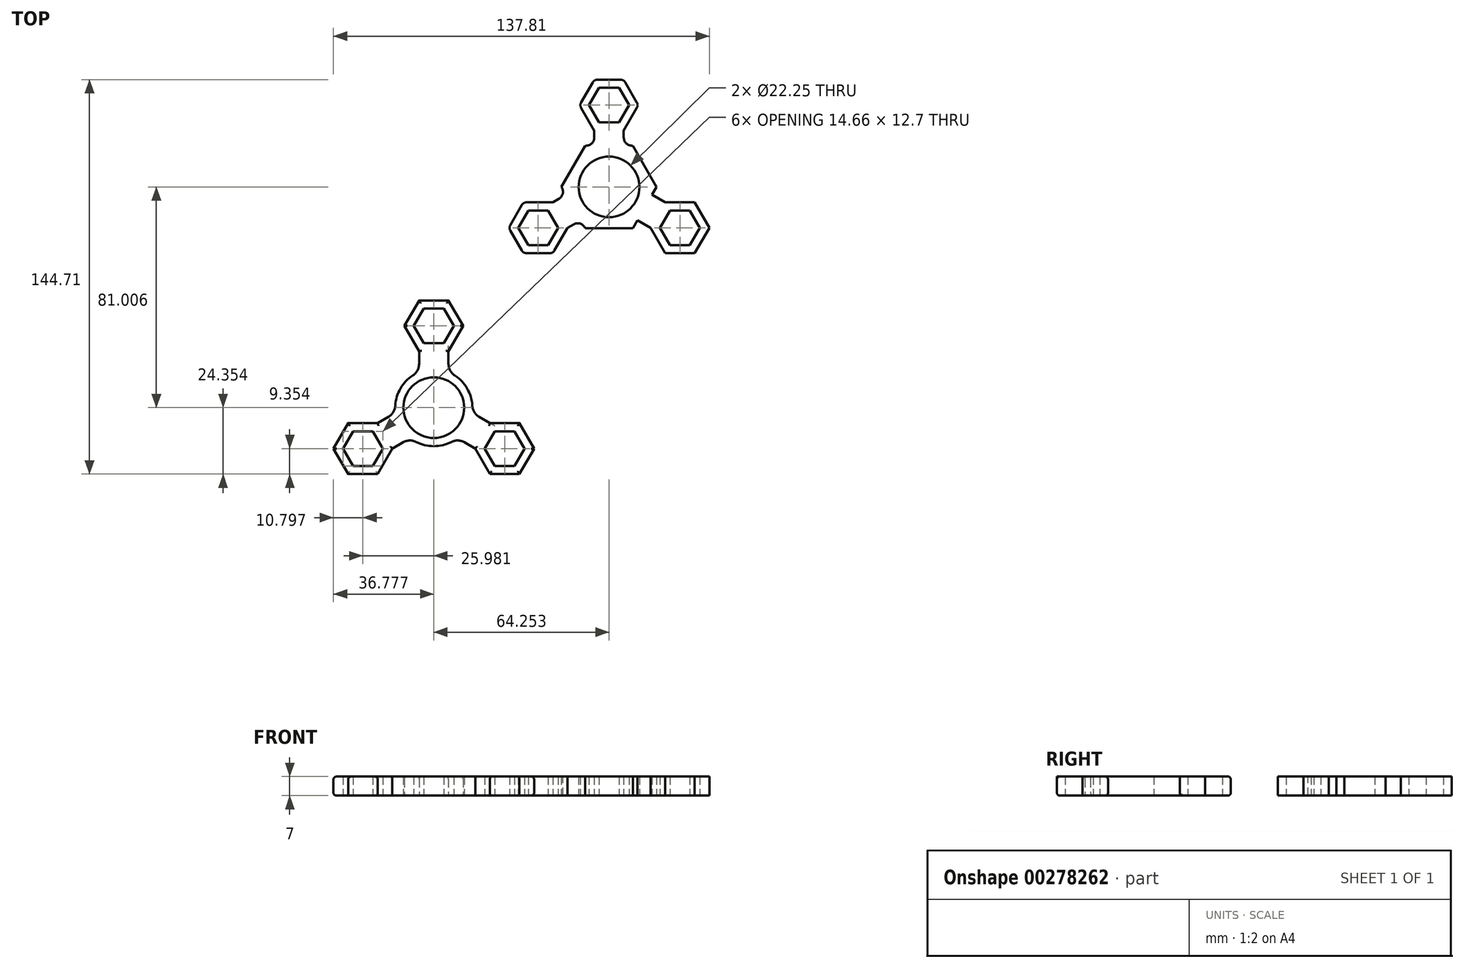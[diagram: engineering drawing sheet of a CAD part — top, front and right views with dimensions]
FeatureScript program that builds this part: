
annotation { "Feature Type Name" : "Feature", "Feature Type Description" : "" }
export const myFeature = defineFeature(function(context is Context, id is Id, definition is map)
    precondition{}
    {
        {
            var Q0;
            Q0=qCreatedBy(makeId("Top.planeOp"),FACE);
            var sketch = newSketch(context, id + "F0", { "sketchPlane" : qUnion([Q0])});
            skCircle(sketch, "E0", {"center": v(-64.25, -81) * mm, "radius": 11.12 * mm});
            skPoint(sketch, "E1.0.midPoint", {"position": v(-64.25, -57.36) * mm});
            skCircle(sketch, "E2.cCircle", {"center": v(-64.25, -51) * mm, "radius": 6.35 * mm, "construction": true});
            skLineSegment(sketch, "E2.0", {"start": v(-67.92, -44.66) * mm, "end": v(-60.59, -44.66) * mm});
            skLineSegment(sketch, "E2.1", {"start": v(-60.59, -44.66) * mm, "end": v(-56.92, -51) * mm});
            skLineSegment(sketch, "E2.2", {"start": v(-56.92, -51) * mm, "end": v(-60.59, -57.36) * mm});
            skLineSegment(sketch, "E2.3", {"start": v(-60.59, -57.36) * mm, "end": v(-67.92, -57.36) * mm});
            skLineSegment(sketch, "E2.4", {"start": v(-67.92, -57.36) * mm, "end": v(-71.58, -51) * mm});
            skLineSegment(sketch, "E2.5", {"start": v(-71.58, -51) * mm, "end": v(-67.92, -44.66) * mm});
            skPoint(sketch, "E2.0.midPoint", {"position": v(-64.25, -44.66) * mm});
            skPoint(sketch, "E3", {"position": v(-74.25, -51) * mm});
            skPoint(sketch, "E4", {"position": v(-54.25, -51) * mm});
            skLineSegment(sketch, "E5", {"start": v(-64.25, -51) * mm, "end": v(-64.25, -69.88) * mm});
            skLineSegment(sketch, "E6", {"start": v(-74.25, -51) * mm, "end": v(-54.25, -51) * mm});
            skLineSegment(sketch, "E7", {"start": v(-64.25, -81) * mm, "end": v(-64.25, -69.88) * mm});
            skCircle(sketch, "E8.cCircle", {"center": v(-64.25, -51) * mm, "radius": 9.35 * mm, "construction": true});
            skLineSegment(sketch, "E8.0", {"start": v(-58.85, -60.36) * mm, "end": v(-69.65, -60.36) * mm});
            skLineSegment(sketch, "E8.1", {"start": v(-69.65, -60.36) * mm, "end": v(-75.05, -51) * mm});
            skLineSegment(sketch, "E8.2", {"start": v(-75.05, -51) * mm, "end": v(-69.65, -41.66) * mm});
            skLineSegment(sketch, "E8.3", {"start": v(-69.65, -41.66) * mm, "end": v(-58.85, -41.66) * mm});
            skLineSegment(sketch, "E8.4", {"start": v(-58.85, -41.66) * mm, "end": v(-53.46, -51) * mm});
            skLineSegment(sketch, "E8.5", {"start": v(-53.46, -51) * mm, "end": v(-58.85, -60.36) * mm});
            skPoint(sketch, "E8.0.midPoint", {"position": v(-64.25, -60.36) * mm});
            skLineSegment(sketch, "E9", {"start": v(-58.85, -60.36) * mm, "end": v(-58.85, -71.28) * mm});
            skLineSegment(sketch, "E10", {"start": v(-58.85, -71.28) * mm, "end": v(-69.65, -71.28) * mm});
            skLineSegment(sketch, "E11", {"start": v(-69.65, -71.28) * mm, "end": v(-69.65, -60.36) * mm});
            skLineSegment(sketch, "E12", {"start": v(-64.25, -81) * mm, "end": v(-64.25, -41.66) * mm});
            skPoint(sketch, "E13.0.midPoint", {"position": v(-64.25, -66.88) * mm});
            skCircle(sketch, "E14", {"center": v(-64.25, -81) * mm, "radius": 14.12 * mm});
            skPoint(sketch, "E15.1.1", {"position": v(-95.73, -99.18) * mm});
            skLineSegment(sketch, "E15.1.3", {"start": v(-84.84, -86.66) * mm, "end": v(-75.38, -81.2) * mm});
            skLineSegment(sketch, "E15.1.4", {"start": v(-64.25, -81) * mm, "end": v(-98.33, -100.68) * mm});
            skLineSegment(sketch, "E15.1.5", {"start": v(-95.63, -105.36) * mm, "end": v(-101.03, -96) * mm});
            skPoint(sketch, "E15.1.6", {"position": v(-95.23, -87.35) * mm});
            skCircle(sketch, "E15.1.7", {"center": v(-90.23, -96) * mm, "radius": 9.35 * mm, "construction": true});
            skPoint(sketch, "E15.1.8", {"position": v(-76.49, -88.07) * mm});
            skPoint(sketch, "E15.1.9", {"position": v(-85.23, -104.67) * mm});
            skLineSegment(sketch, "E15.1.10", {"start": v(-82.9, -96) * mm, "end": v(-86.57, -102.36) * mm});
            skLineSegment(sketch, "E15.1.11", {"start": v(-101.03, -96) * mm, "end": v(-95.63, -86.66) * mm});
            skLineSegment(sketch, "E15.1.12", {"start": v(-84.84, -105.36) * mm, "end": v(-95.63, -105.36) * mm});
            skLineSegment(sketch, "E15.1.13", {"start": v(-85.23, -104.67) * mm, "end": v(-95.23, -87.35) * mm});
            skPoint(sketch, "E15.1.14", {"position": v(-82.14, -91.33) * mm});
            skLineSegment(sketch, "E15.1.15", {"start": v(-84.84, -86.66) * mm, "end": v(-79.44, -96) * mm});
            skLineSegment(sketch, "E15.1.16", {"start": v(-69.98, -90.54) * mm, "end": v(-79.44, -96) * mm});
            skLineSegment(sketch, "E15.1.17", {"start": v(-79.44, -96) * mm, "end": v(-84.84, -105.36) * mm});
            skLineSegment(sketch, "E15.1.19", {"start": v(-95.63, -86.66) * mm, "end": v(-84.84, -86.66) * mm});
            skLineSegment(sketch, "E15.1.20", {"start": v(-75.38, -81.2) * mm, "end": v(-69.98, -90.54) * mm});
            skPoint(sketch, "E15.1.21", {"position": v(-84.73, -92.83) * mm});
            skCircle(sketch, "E15.1.22", {"center": v(-90.23, -96) * mm, "radius": 6.35 * mm, "construction": true});
            skPoint(sketch, "E15.1.23", {"position": v(-90.23, -96) * mm});
            skLineSegment(sketch, "E15.1.24", {"start": v(-93.9, -89.66) * mm, "end": v(-86.57, -89.66) * mm});
            skLineSegment(sketch, "E15.1.25", {"start": v(-86.57, -89.66) * mm, "end": v(-82.9, -96) * mm});
            skLineSegment(sketch, "E15.1.26", {"start": v(-64.25, -81) * mm, "end": v(-73.89, -86.57) * mm});
            skLineSegment(sketch, "E15.1.29", {"start": v(-97.57, -96) * mm, "end": v(-93.9, -89.66) * mm});
            skLineSegment(sketch, "E15.1.30", {"start": v(-86.57, -102.36) * mm, "end": v(-93.9, -102.36) * mm});
            skLineSegment(sketch, "E15.1.31", {"start": v(-90.23, -96) * mm, "end": v(-73.89, -86.57) * mm});
            skLineSegment(sketch, "E15.1.32", {"start": v(-93.9, -102.36) * mm, "end": v(-97.57, -96) * mm});
            skPoint(sketch, "E15.2.1", {"position": v(-32.77, -99.18) * mm});
            skLineSegment(sketch, "E15.2.3", {"start": v(-49.07, -96) * mm, "end": v(-58.53, -90.54) * mm});
            skLineSegment(sketch, "E15.2.4", {"start": v(-64.25, -81) * mm, "end": v(-30.17, -100.68) * mm});
            skLineSegment(sketch, "E15.2.5", {"start": v(-27.48, -96) * mm, "end": v(-32.87, -105.36) * mm});
            skPoint(sketch, "E15.2.6", {"position": v(-43.27, -104.67) * mm});
            skCircle(sketch, "E15.2.7", {"center": v(-38.27, -96) * mm, "radius": 9.35 * mm, "construction": true});
            skPoint(sketch, "E15.2.8", {"position": v(-52.02, -88.07) * mm});
            skPoint(sketch, "E15.2.9", {"position": v(-33.27, -87.35) * mm});
            skLineSegment(sketch, "E15.2.10", {"start": v(-41.94, -89.66) * mm, "end": v(-34.6, -89.66) * mm});
            skLineSegment(sketch, "E15.2.11", {"start": v(-32.87, -105.36) * mm, "end": v(-43.67, -105.36) * mm});
            skLineSegment(sketch, "E15.2.12", {"start": v(-32.87, -86.66) * mm, "end": v(-27.48, -96) * mm});
            skLineSegment(sketch, "E15.2.13", {"start": v(-33.27, -87.35) * mm, "end": v(-43.27, -104.67) * mm});
            skPoint(sketch, "E15.2.14", {"position": v(-46.37, -91.33) * mm});
            skLineSegment(sketch, "E15.2.15", {"start": v(-49.07, -96) * mm, "end": v(-43.67, -86.66) * mm});
            skLineSegment(sketch, "E15.2.16", {"start": v(-53.13, -81.2) * mm, "end": v(-43.67, -86.66) * mm});
            skLineSegment(sketch, "E15.2.17", {"start": v(-43.67, -86.66) * mm, "end": v(-32.87, -86.66) * mm});
            skLineSegment(sketch, "E15.2.19", {"start": v(-43.67, -105.36) * mm, "end": v(-49.07, -96) * mm});
            skLineSegment(sketch, "E15.2.20", {"start": v(-58.53, -90.54) * mm, "end": v(-53.13, -81.2) * mm});
            skPoint(sketch, "E15.2.21", {"position": v(-43.77, -92.83) * mm});
            skCircle(sketch, "E15.2.22", {"center": v(-38.27, -96) * mm, "radius": 6.35 * mm, "construction": true});
            skPoint(sketch, "E15.2.23", {"position": v(-38.27, -96) * mm});
            skLineSegment(sketch, "E15.2.24", {"start": v(-41.94, -102.36) * mm, "end": v(-45.6, -96) * mm});
            skLineSegment(sketch, "E15.2.25", {"start": v(-45.6, -96) * mm, "end": v(-41.94, -89.66) * mm});
            skLineSegment(sketch, "E15.2.26", {"start": v(-64.25, -81) * mm, "end": v(-54.62, -86.57) * mm});
            skLineSegment(sketch, "E15.2.29", {"start": v(-34.6, -102.36) * mm, "end": v(-41.94, -102.36) * mm});
            skLineSegment(sketch, "E15.2.30", {"start": v(-34.6, -89.66) * mm, "end": v(-30.94, -96) * mm});
            skLineSegment(sketch, "E15.2.31", {"start": v(-38.27, -96) * mm, "end": v(-54.62, -86.57) * mm});
            skLineSegment(sketch, "E15.2.32", {"start": v(-30.94, -96) * mm, "end": v(-34.6, -102.36) * mm});
            skSolve(sketch);
        }
        {
            var Q0;
            Q0=qCreatedBy(makeId("Top.planeOp"),FACE);
            var sketch = newSketch(context, id + "F1", { "sketchPlane" : qUnion([Q0])});
            skCircle(sketch, "E16", {"center": v(0, 0) * mm, "radius": 11.12 * mm});
            skPoint(sketch, "E17.0.midPoint", {"position": v(0, 23.65) * mm});
            skCircle(sketch, "E18.cCircle", {"center": v(0, 30) * mm, "radius": 6.35 * mm, "construction": true});
            skLineSegment(sketch, "E18.0", {"start": v(-3.67, 36.35) * mm, "end": v(3.67, 36.35) * mm});
            skLineSegment(sketch, "E18.1", {"start": v(3.67, 36.35) * mm, "end": v(7.33, 30) * mm});
            skLineSegment(sketch, "E18.2", {"start": v(7.33, 30) * mm, "end": v(3.67, 23.65) * mm});
            skLineSegment(sketch, "E18.3", {"start": v(3.67, 23.65) * mm, "end": v(-3.67, 23.65) * mm});
            skLineSegment(sketch, "E18.4", {"start": v(-3.67, 23.65) * mm, "end": v(-7.33, 30) * mm});
            skLineSegment(sketch, "E18.5", {"start": v(-7.33, 30) * mm, "end": v(-3.67, 36.35) * mm});
            skPoint(sketch, "E18.0.midPoint", {"position": v(0, 36.35) * mm});
            skPoint(sketch, "E19", {"position": v(-10, 30) * mm});
            skPoint(sketch, "E20", {"position": v(10, 30) * mm});
            skLineSegment(sketch, "E21", {"start": v(0, 30) * mm, "end": v(0, 11.12) * mm});
            skLineSegment(sketch, "E22", {"start": v(-10, 30) * mm, "end": v(10, 30) * mm});
            skLineSegment(sketch, "E23", {"start": v(0, 0) * mm, "end": v(0, 11.12) * mm});
            skCircle(sketch, "E24.cCircle", {"center": v(0, 30) * mm, "radius": 9.35 * mm, "construction": true});
            skLineSegment(sketch, "E24.0", {"start": v(5.4, 20.65) * mm, "end": v(-5.4, 20.65) * mm});
            skLineSegment(sketch, "E24.1", {"start": v(-5.4, 20.65) * mm, "end": v(-10.8, 30) * mm});
            skLineSegment(sketch, "E24.2", {"start": v(-10.8, 30) * mm, "end": v(-5.4, 39.35) * mm});
            skLineSegment(sketch, "E24.3", {"start": v(-5.4, 39.35) * mm, "end": v(5.4, 39.35) * mm});
            skLineSegment(sketch, "E24.4", {"start": v(5.4, 39.35) * mm, "end": v(10.8, 30) * mm});
            skLineSegment(sketch, "E24.5", {"start": v(10.8, 30) * mm, "end": v(5.4, 20.65) * mm});
            skPoint(sketch, "E24.0.midPoint", {"position": v(0, 20.65) * mm});
            skLineSegment(sketch, "E25", {"start": v(5.4, 20.65) * mm, "end": v(5.4, 9.73) * mm});
            skLineSegment(sketch, "E26", {"start": v(5.4, 9.73) * mm, "end": v(-5.4, 9.73) * mm});
            skLineSegment(sketch, "E27", {"start": v(-5.4, 9.73) * mm, "end": v(-5.4, 20.65) * mm});
            skLineSegment(sketch, "E28", {"start": v(0, 0) * mm, "end": v(0, 39.35) * mm});
            skCircle(sketch, "E29.cCircle", {"center": v(0, 0) * mm, "radius": 15.13 * mm, "construction": true});
            skLineSegment(sketch, "E29.0", {"start": v(-8.73, 15.12) * mm, "end": v(8.73, 15.13) * mm});
            skLineSegment(sketch, "E29.1", {"start": v(8.73, 15.13) * mm, "end": v(17.46, 0) * mm});
            skLineSegment(sketch, "E29.2", {"start": v(17.46, 0) * mm, "end": v(8.73, -15.12) * mm});
            skLineSegment(sketch, "E29.3", {"start": v(8.73, -15.12) * mm, "end": v(-8.73, -15.13) * mm});
            skLineSegment(sketch, "E29.4", {"start": v(-8.73, -15.13) * mm, "end": v(-17.46, 0) * mm});
            skLineSegment(sketch, "E29.5", {"start": v(-17.46, 0) * mm, "end": v(-8.73, 15.12) * mm});
            skPoint(sketch, "E29.0.midPoint", {"position": v(0, 15.13) * mm});
            skPoint(sketch, "E30.1.1", {"position": v(-20.48, -11.83) * mm});
            skPoint(sketch, "E30.1.2", {"position": v(-25.98, -15) * mm});
            skLineSegment(sketch, "E30.1.4", {"start": v(-20.98, -23.66) * mm, "end": v(-30.98, -6.34) * mm});
            skLineSegment(sketch, "E30.1.6", {"start": v(17.46, 0) * mm, "end": v(8.73, -15.13) * mm});
            skPoint(sketch, "E30.1.7", {"position": v(-30.98, -6.34) * mm});
            skLineSegment(sketch, "E30.1.8", {"start": v(-5.73, -9.54) * mm, "end": v(-15.18, -15) * mm});
            skPoint(sketch, "E30.1.9", {"position": v(-17.88, -10.32) * mm});
            skLineSegment(sketch, "E30.1.10", {"start": v(-15.18, -15) * mm, "end": v(-20.58, -24.35) * mm});
            skLineSegment(sketch, "E30.1.12", {"start": v(-11.12, -0.19) * mm, "end": v(-5.73, -9.54) * mm});
            skLineSegment(sketch, "E30.1.15", {"start": v(-20.58, -5.65) * mm, "end": v(-11.12, -0.19) * mm});
            skLineSegment(sketch, "E30.1.17", {"start": v(-31.38, -5.65) * mm, "end": v(-20.58, -5.65) * mm});
            skCircle(sketch, "E30.1.18", {"center": v(-25.98, -15) * mm, "radius": 9.35 * mm, "construction": true});
            skCircle(sketch, "E30.1.19", {"center": v(-25.98, -15) * mm, "radius": 6.35 * mm, "construction": true});
            skPoint(sketch, "E30.1.20", {"position": v(-13.1, -7.56) * mm});
            skLineSegment(sketch, "E30.1.22", {"start": v(0, 0) * mm, "end": v(-34.08, -19.68) * mm});
            skPoint(sketch, "E30.1.23", {"position": v(-20.98, -23.66) * mm});
            skPoint(sketch, "E30.1.24", {"position": v(-31.48, -18.17) * mm});
            skLineSegment(sketch, "E30.1.26", {"start": v(-33.31, -15) * mm, "end": v(-29.65, -8.65) * mm});
            skLineSegment(sketch, "E30.1.27", {"start": v(-22.31, -21.35) * mm, "end": v(-29.65, -21.35) * mm});
            skLineSegment(sketch, "E30.1.28", {"start": v(-20.58, -24.35) * mm, "end": v(-31.38, -24.35) * mm});
            skLineSegment(sketch, "E30.1.29", {"start": v(-36.78, -15) * mm, "end": v(-31.38, -5.65) * mm});
            skLineSegment(sketch, "E30.1.30", {"start": v(-18.65, -15) * mm, "end": v(-22.31, -21.35) * mm});
            skLineSegment(sketch, "E30.1.31", {"start": v(-31.38, -24.35) * mm, "end": v(-36.78, -15) * mm});
            skLineSegment(sketch, "E30.1.32", {"start": v(-25.98, -15) * mm, "end": v(-9.63, -5.56) * mm});
            skLineSegment(sketch, "E30.1.34", {"start": v(0, 0) * mm, "end": v(-9.63, -5.56) * mm});
            skLineSegment(sketch, "E30.1.35", {"start": v(-22.31, -8.65) * mm, "end": v(-18.65, -15) * mm});
            skLineSegment(sketch, "E30.1.36", {"start": v(-29.65, -21.35) * mm, "end": v(-33.31, -15) * mm});
            skLineSegment(sketch, "E30.1.37", {"start": v(-20.58, -5.65) * mm, "end": v(-15.18, -15) * mm});
            skLineSegment(sketch, "E30.1.38", {"start": v(-29.65, -8.65) * mm, "end": v(-22.31, -8.65) * mm});
            skPoint(sketch, "E31.3.2.0", {"position": v(20.48, -11.83) * mm});
            skPoint(sketch, "E31.4.2.0", {"position": v(25.98, -15) * mm});
            skLineSegment(sketch, "E31.8.2.0", {"start": v(30.98, -6.34) * mm, "end": v(20.98, -23.66) * mm});
            skLineSegment(sketch, "E31.13.2.0", {"start": v(-8.73, 15.13) * mm, "end": v(8.73, 15.13) * mm});
            skPoint(sketch, "E31.16.2.0", {"position": v(20.98, -23.66) * mm});
            skLineSegment(sketch, "E31.17.2.0", {"start": v(11.12, -0.19) * mm, "end": v(20.58, -5.65) * mm});
            skPoint(sketch, "E31.20.2.0", {"position": v(17.88, -10.33) * mm});
            skLineSegment(sketch, "E31.21.2.0", {"start": v(20.58, -5.65) * mm, "end": v(31.38, -5.65) * mm});
            skLineSegment(sketch, "E31.25.2.0", {"start": v(5.73, -9.54) * mm, "end": v(11.12, -0.19) * mm});
            skLineSegment(sketch, "E31.33.2.0", {"start": v(15.18, -15) * mm, "end": v(5.73, -9.54) * mm});
            skLineSegment(sketch, "E31.39.2.0", {"start": v(20.58, -24.35) * mm, "end": v(15.18, -15) * mm});
            skCircle(sketch, "E31.42.2.0", {"center": v(25.98, -15) * mm, "radius": 9.35 * mm, "construction": true});
            skCircle(sketch, "E31.44.2.0", {"center": v(25.98, -15) * mm, "radius": 6.35 * mm, "construction": true});
            skPoint(sketch, "E31.46.2.0", {"position": v(13.1, -7.56) * mm});
            skLineSegment(sketch, "E31.50.2.0", {"start": v(0, 0) * mm, "end": v(34.08, -19.68) * mm});
            skPoint(sketch, "E31.53.2.0", {"position": v(30.98, -6.34) * mm});
            skPoint(sketch, "E31.54.2.0", {"position": v(31.48, -18.18) * mm});
            skLineSegment(sketch, "E31.56.2.0", {"start": v(29.65, -21.35) * mm, "end": v(22.31, -21.35) * mm});
            skLineSegment(sketch, "E31.59.2.0", {"start": v(29.65, -8.65) * mm, "end": v(33.31, -15) * mm});
            skLineSegment(sketch, "E31.62.2.0", {"start": v(31.38, -5.65) * mm, "end": v(36.78, -15) * mm});
            skLineSegment(sketch, "E31.65.2.0", {"start": v(31.38, -24.35) * mm, "end": v(20.58, -24.35) * mm});
            skLineSegment(sketch, "E31.68.2.0", {"start": v(22.31, -8.65) * mm, "end": v(29.65, -8.65) * mm});
            skLineSegment(sketch, "E31.71.2.0", {"start": v(36.78, -15) * mm, "end": v(31.38, -24.35) * mm});
            skLineSegment(sketch, "E31.74.2.0", {"start": v(25.98, -15) * mm, "end": v(9.63, -5.56) * mm});
            skLineSegment(sketch, "E31.79.2.0", {"start": v(0, 0) * mm, "end": v(9.63, -5.56) * mm});
            skLineSegment(sketch, "E31.82.2.0", {"start": v(18.65, -15) * mm, "end": v(22.31, -8.65) * mm});
            skLineSegment(sketch, "E31.85.2.0", {"start": v(33.31, -15) * mm, "end": v(29.65, -21.35) * mm});
            skLineSegment(sketch, "E31.88.2.0", {"start": v(15.18, -15) * mm, "end": v(20.58, -5.65) * mm});
            skLineSegment(sketch, "E31.91.2.0", {"start": v(22.31, -21.35) * mm, "end": v(18.65, -15) * mm});
            skSolve(sketch);
        }
        {
            var Q0;
            Q0 = qSketchRegion(id + "F0", true);
            extrude(context, id + "F2", {"entities" : qUnion([Q0]), "depth" : 7 * mm, "offsetDistance" : 25 * mm});
        }
        {
            var Q0;
            Q0=makeQuery(id+"F2.opExtrude","SWEPT_EDGE",EDGE,{"disambiguationData":[OSD([sQuery(id+"F0.wireOp",EDGE,"E9"),sQuery(id+"F0.wireOp",EDGE,"E14")])]});
            var Q1;
            Q1=makeQuery(id+"F2.opExtrude","SWEPT_EDGE",EDGE,{"disambiguationData":[OSD([sQuery(id+"F0.wireOp",EDGE,"E14"),sQuery(id+"F0.wireOp",EDGE,"E15.2.16")])]});
            var Q2;
            Q2=makeQuery(id+"F2.opExtrude","SWEPT_EDGE",EDGE,{"disambiguationData":[OSD([sQuery(id+"F0.wireOp",EDGE,"E14"),sQuery(id+"F0.wireOp",EDGE,"E15.2.3")])]});
            var Q3;
            Q3=makeQuery(id+"F2.opExtrude","SWEPT_EDGE",EDGE,{"disambiguationData":[OSD([sQuery(id+"F0.wireOp",EDGE,"E15.1.16"),sQuery(id+"F0.wireOp",EDGE,"E14")])]});
            var Q4;
            Q4=makeQuery(id+"F2.opExtrude","SWEPT_EDGE",EDGE,{"disambiguationData":[OSD([sQuery(id+"F0.wireOp",EDGE,"E15.1.3"),sQuery(id+"F0.wireOp",EDGE,"E14")])]});
            var Q5;
            Q5=makeQuery(id+"F2.opExtrude","SWEPT_EDGE",EDGE,{"disambiguationData":[OSD([sQuery(id+"F0.wireOp",EDGE,"E11"),sQuery(id+"F0.wireOp",EDGE,"E14")])]});
            fillet(context, id + "F3", {"entities" : qUnion([Q0, Q1, Q2, Q3, Q4, Q5]), "radius" : 5 * mm, "tangentPropagation" : true, "allowEdgeOverflow" : false});
        }
        {
            var Q0;
            Q0=makeQuery(id+"F2.opExtrude","CAP_EDGE",EDGE,{"disambiguationData":[OSD([sQuery(id+"F0.wireOp",EDGE,"E15.2.19")])],"isStart":false});
            var Q1;
            Q1=makeQuery(id+"F2.opExtrude","CAP_EDGE",EDGE,{"disambiguationData":[OSD([sQuery(id+"F0.wireOp",EDGE,"E15.2.5")])],"isStart":false});
            var Q2;
            Q2=makeQuery(id+"F2.opExtrude","CAP_EDGE",EDGE,{"disambiguationData":[OSD([sQuery(id+"F0.wireOp",EDGE,"E15.2.12")])],"isStart":false});
            var Q3;
            Q3=makeQuery(id+"F2.opExtrude","CAP_EDGE",EDGE,{"disambiguationData":[OSD([sQuery(id+"F0.wireOp",EDGE,"E15.2.11")])],"isStart":false});
            var Q4;
            Q4=makeQuery(id+"F2.opExtrude","CAP_EDGE",EDGE,{"disambiguationData":[OSD([sQuery(id+"F0.wireOp",EDGE,"E15.2.17")])],"isStart":false});
            var Q5;
            {var subQ0=sQuery(id+"F0.wireOp",EDGE,"E15.2.16");var subQ1=sQuery(id+"F0.wireOp",EDGE,"E14");Q5=makeQuery(id+"F3.opFillet","BLEND_EDGE",EDGE,{"blendedFrom":[makeQuery(id+"F2.opExtrude","SWEPT_EDGE",EDGE,{"disambiguationData":[OSD([subQ1,subQ0])]}),makeQuery(id+"F2.opExtrude","CAP_FACE",FACE,{"disambiguationData":[OSD([sQuery(id+"F0.wireOp",EDGE,"E2.0"),sQuery(id+"F0.wireOp",EDGE,"E2.1"),sQuery(id+"F0.wireOp",EDGE,"E2.2"),sQuery(id+"F0.wireOp",EDGE,"E2.3"),sQuery(id+"F0.wireOp",EDGE,"E2.4"),sQuery(id+"F0.wireOp",EDGE,"E2.5"),sQuery(id+"F0.wireOp",EDGE,"E8.1"),sQuery(id+"F0.wireOp",EDGE,"E8.2"),sQuery(id+"F0.wireOp",EDGE,"E8.3"),sQuery(id+"F0.wireOp",EDGE,"E8.4"),sQuery(id+"F0.wireOp",EDGE,"E8.5"),sQuery(id+"F0.wireOp",EDGE,"E9"),sQuery(id+"F0.wireOp",EDGE,"E11"),sQuery(id+"F0.wireOp",EDGE,"E15.1.3"),sQuery(id+"F0.wireOp",EDGE,"E15.1.5"),sQuery(id+"F0.wireOp",EDGE,"E15.1.10"),sQuery(id+"F0.wireOp",EDGE,"E15.1.11"),sQuery(id+"F0.wireOp",EDGE,"E15.1.12"),sQuery(id+"F0.wireOp",EDGE,"E15.1.16"),sQuery(id+"F0.wireOp",EDGE,"E15.1.17"),sQuery(id+"F0.wireOp",EDGE,"E15.1.19"),sQuery(id+"F0.wireOp",EDGE,"E15.1.24"),sQuery(id+"F0.wireOp",EDGE,"E15.1.25"),sQuery(id+"F0.wireOp",EDGE,"E15.1.29"),sQuery(id+"F0.wireOp",EDGE,"E15.1.30"),sQuery(id+"F0.wireOp",EDGE,"E15.1.32"),subQ1,sQuery(id+"F0.wireOp",EDGE,"E15.2.3"),sQuery(id+"F0.wireOp",EDGE,"E15.2.5"),sQuery(id+"F0.wireOp",EDGE,"E15.2.10"),sQuery(id+"F0.wireOp",EDGE,"E15.2.11"),sQuery(id+"F0.wireOp",EDGE,"E15.2.12"),subQ0,sQuery(id+"F0.wireOp",EDGE,"E15.2.17"),sQuery(id+"F0.wireOp",EDGE,"E15.2.19"),sQuery(id+"F0.wireOp",EDGE,"E15.2.24"),sQuery(id+"F0.wireOp",EDGE,"E15.2.25"),sQuery(id+"F0.wireOp",EDGE,"E15.2.29"),sQuery(id+"F0.wireOp",EDGE,"E15.2.30"),sQuery(id+"F0.wireOp",EDGE,"E15.2.32"),sQuery(id+"F0.wireOp",EDGE,"E0")])],"isStart":false})],"blendedInto":[makeQuery(id+"F2.opExtrude","CAP_FACE",FACE,{"disambiguationData":[OSD([sQuery(id+"F0.wireOp",EDGE,"E2.0"),sQuery(id+"F0.wireOp",EDGE,"E2.1"),sQuery(id+"F0.wireOp",EDGE,"E2.2"),sQuery(id+"F0.wireOp",EDGE,"E2.3"),sQuery(id+"F0.wireOp",EDGE,"E2.4"),sQuery(id+"F0.wireOp",EDGE,"E2.5"),sQuery(id+"F0.wireOp",EDGE,"E8.1"),sQuery(id+"F0.wireOp",EDGE,"E8.2"),sQuery(id+"F0.wireOp",EDGE,"E8.3"),sQuery(id+"F0.wireOp",EDGE,"E8.4"),sQuery(id+"F0.wireOp",EDGE,"E8.5"),sQuery(id+"F0.wireOp",EDGE,"E9"),sQuery(id+"F0.wireOp",EDGE,"E11"),sQuery(id+"F0.wireOp",EDGE,"E15.1.3"),sQuery(id+"F0.wireOp",EDGE,"E15.1.5"),sQuery(id+"F0.wireOp",EDGE,"E15.1.10"),sQuery(id+"F0.wireOp",EDGE,"E15.1.11"),sQuery(id+"F0.wireOp",EDGE,"E15.1.12"),sQuery(id+"F0.wireOp",EDGE,"E15.1.16"),sQuery(id+"F0.wireOp",EDGE,"E15.1.17"),sQuery(id+"F0.wireOp",EDGE,"E15.1.19"),sQuery(id+"F0.wireOp",EDGE,"E15.1.24"),sQuery(id+"F0.wireOp",EDGE,"E15.1.25"),sQuery(id+"F0.wireOp",EDGE,"E15.1.29"),sQuery(id+"F0.wireOp",EDGE,"E15.1.30"),sQuery(id+"F0.wireOp",EDGE,"E15.1.32"),subQ1,sQuery(id+"F0.wireOp",EDGE,"E15.2.3"),sQuery(id+"F0.wireOp",EDGE,"E15.2.5"),sQuery(id+"F0.wireOp",EDGE,"E15.2.10"),sQuery(id+"F0.wireOp",EDGE,"E15.2.11"),sQuery(id+"F0.wireOp",EDGE,"E15.2.12"),subQ0,sQuery(id+"F0.wireOp",EDGE,"E15.2.17"),sQuery(id+"F0.wireOp",EDGE,"E15.2.19"),sQuery(id+"F0.wireOp",EDGE,"E15.2.24"),sQuery(id+"F0.wireOp",EDGE,"E15.2.25"),sQuery(id+"F0.wireOp",EDGE,"E15.2.29"),sQuery(id+"F0.wireOp",EDGE,"E15.2.30"),sQuery(id+"F0.wireOp",EDGE,"E15.2.32"),sQuery(id+"F0.wireOp",EDGE,"E0")])],"isStart":false})]});}
            var Q6;
            Q6=makeQuery(id+"F2.opExtrude","CAP_EDGE",EDGE,{"disambiguationData":[OSD([sQuery(id+"F0.wireOp",EDGE,"E8.5")])],"isStart":false});
            var Q7;
            Q7=makeQuery(id+"F2.opExtrude","CAP_EDGE",EDGE,{"disambiguationData":[OSD([sQuery(id+"F0.wireOp",EDGE,"E8.4")])],"isStart":false});
            var Q8;
            Q8=makeQuery(id+"F2.opExtrude","CAP_EDGE",EDGE,{"disambiguationData":[OSD([sQuery(id+"F0.wireOp",EDGE,"E8.3")])],"isStart":false});
            var Q9;
            Q9=makeQuery(id+"F2.opExtrude","CAP_EDGE",EDGE,{"disambiguationData":[OSD([sQuery(id+"F0.wireOp",EDGE,"E8.2")])],"isStart":false});
            var Q10;
            Q10=makeQuery(id+"F2.opExtrude","CAP_EDGE",EDGE,{"disambiguationData":[OSD([sQuery(id+"F0.wireOp",EDGE,"E8.1")])],"isStart":false});
            var Q11;
            {var subQ0=sQuery(id+"F0.wireOp",EDGE,"E14");var subQ1=sQuery(id+"F0.wireOp",EDGE,"E11");Q11=makeQuery(id+"F3.opFillet","BLEND_EDGE",EDGE,{"blendedFrom":[makeQuery(id+"F2.opExtrude","SWEPT_EDGE",EDGE,{"disambiguationData":[OSD([subQ1,subQ0])]}),makeQuery(id+"F2.opExtrude","CAP_FACE",FACE,{"disambiguationData":[OSD([sQuery(id+"F0.wireOp",EDGE,"E2.0"),sQuery(id+"F0.wireOp",EDGE,"E2.1"),sQuery(id+"F0.wireOp",EDGE,"E2.2"),sQuery(id+"F0.wireOp",EDGE,"E2.3"),sQuery(id+"F0.wireOp",EDGE,"E2.4"),sQuery(id+"F0.wireOp",EDGE,"E2.5"),sQuery(id+"F0.wireOp",EDGE,"E8.1"),sQuery(id+"F0.wireOp",EDGE,"E8.2"),sQuery(id+"F0.wireOp",EDGE,"E8.3"),sQuery(id+"F0.wireOp",EDGE,"E8.4"),sQuery(id+"F0.wireOp",EDGE,"E8.5"),sQuery(id+"F0.wireOp",EDGE,"E9"),subQ1,sQuery(id+"F0.wireOp",EDGE,"E15.1.3"),sQuery(id+"F0.wireOp",EDGE,"E15.1.5"),sQuery(id+"F0.wireOp",EDGE,"E15.1.10"),sQuery(id+"F0.wireOp",EDGE,"E15.1.11"),sQuery(id+"F0.wireOp",EDGE,"E15.1.12"),sQuery(id+"F0.wireOp",EDGE,"E15.1.16"),sQuery(id+"F0.wireOp",EDGE,"E15.1.17"),sQuery(id+"F0.wireOp",EDGE,"E15.1.19"),sQuery(id+"F0.wireOp",EDGE,"E15.1.24"),sQuery(id+"F0.wireOp",EDGE,"E15.1.25"),sQuery(id+"F0.wireOp",EDGE,"E15.1.29"),sQuery(id+"F0.wireOp",EDGE,"E15.1.30"),sQuery(id+"F0.wireOp",EDGE,"E15.1.32"),subQ0,sQuery(id+"F0.wireOp",EDGE,"E15.2.3"),sQuery(id+"F0.wireOp",EDGE,"E15.2.5"),sQuery(id+"F0.wireOp",EDGE,"E15.2.10"),sQuery(id+"F0.wireOp",EDGE,"E15.2.11"),sQuery(id+"F0.wireOp",EDGE,"E15.2.12"),sQuery(id+"F0.wireOp",EDGE,"E15.2.16"),sQuery(id+"F0.wireOp",EDGE,"E15.2.17"),sQuery(id+"F0.wireOp",EDGE,"E15.2.19"),sQuery(id+"F0.wireOp",EDGE,"E15.2.24"),sQuery(id+"F0.wireOp",EDGE,"E15.2.25"),sQuery(id+"F0.wireOp",EDGE,"E15.2.29"),sQuery(id+"F0.wireOp",EDGE,"E15.2.30"),sQuery(id+"F0.wireOp",EDGE,"E15.2.32"),sQuery(id+"F0.wireOp",EDGE,"E0")])],"isStart":false})],"blendedInto":[makeQuery(id+"F2.opExtrude","CAP_FACE",FACE,{"disambiguationData":[OSD([sQuery(id+"F0.wireOp",EDGE,"E2.0"),sQuery(id+"F0.wireOp",EDGE,"E2.1"),sQuery(id+"F0.wireOp",EDGE,"E2.2"),sQuery(id+"F0.wireOp",EDGE,"E2.3"),sQuery(id+"F0.wireOp",EDGE,"E2.4"),sQuery(id+"F0.wireOp",EDGE,"E2.5"),sQuery(id+"F0.wireOp",EDGE,"E8.1"),sQuery(id+"F0.wireOp",EDGE,"E8.2"),sQuery(id+"F0.wireOp",EDGE,"E8.3"),sQuery(id+"F0.wireOp",EDGE,"E8.4"),sQuery(id+"F0.wireOp",EDGE,"E8.5"),sQuery(id+"F0.wireOp",EDGE,"E9"),subQ1,sQuery(id+"F0.wireOp",EDGE,"E15.1.3"),sQuery(id+"F0.wireOp",EDGE,"E15.1.5"),sQuery(id+"F0.wireOp",EDGE,"E15.1.10"),sQuery(id+"F0.wireOp",EDGE,"E15.1.11"),sQuery(id+"F0.wireOp",EDGE,"E15.1.12"),sQuery(id+"F0.wireOp",EDGE,"E15.1.16"),sQuery(id+"F0.wireOp",EDGE,"E15.1.17"),sQuery(id+"F0.wireOp",EDGE,"E15.1.19"),sQuery(id+"F0.wireOp",EDGE,"E15.1.24"),sQuery(id+"F0.wireOp",EDGE,"E15.1.25"),sQuery(id+"F0.wireOp",EDGE,"E15.1.29"),sQuery(id+"F0.wireOp",EDGE,"E15.1.30"),sQuery(id+"F0.wireOp",EDGE,"E15.1.32"),subQ0,sQuery(id+"F0.wireOp",EDGE,"E15.2.3"),sQuery(id+"F0.wireOp",EDGE,"E15.2.5"),sQuery(id+"F0.wireOp",EDGE,"E15.2.10"),sQuery(id+"F0.wireOp",EDGE,"E15.2.11"),sQuery(id+"F0.wireOp",EDGE,"E15.2.12"),sQuery(id+"F0.wireOp",EDGE,"E15.2.16"),sQuery(id+"F0.wireOp",EDGE,"E15.2.17"),sQuery(id+"F0.wireOp",EDGE,"E15.2.19"),sQuery(id+"F0.wireOp",EDGE,"E15.2.24"),sQuery(id+"F0.wireOp",EDGE,"E15.2.25"),sQuery(id+"F0.wireOp",EDGE,"E15.2.29"),sQuery(id+"F0.wireOp",EDGE,"E15.2.30"),sQuery(id+"F0.wireOp",EDGE,"E15.2.32"),sQuery(id+"F0.wireOp",EDGE,"E0")])],"isStart":false})]});}
            var Q12;
            {var subQ0=sQuery(id+"F0.wireOp",EDGE,"E14");var subQ1=sQuery(id+"F0.wireOp",EDGE,"E15.1.16");Q12=makeQuery(id+"F3.opFillet","BLEND_EDGE",EDGE,{"blendedFrom":[makeQuery(id+"F2.opExtrude","SWEPT_EDGE",EDGE,{"disambiguationData":[OSD([subQ1,subQ0])]}),makeQuery(id+"F2.opExtrude","CAP_FACE",FACE,{"disambiguationData":[OSD([sQuery(id+"F0.wireOp",EDGE,"E2.0"),sQuery(id+"F0.wireOp",EDGE,"E2.1"),sQuery(id+"F0.wireOp",EDGE,"E2.2"),sQuery(id+"F0.wireOp",EDGE,"E2.3"),sQuery(id+"F0.wireOp",EDGE,"E2.4"),sQuery(id+"F0.wireOp",EDGE,"E2.5"),sQuery(id+"F0.wireOp",EDGE,"E8.1"),sQuery(id+"F0.wireOp",EDGE,"E8.2"),sQuery(id+"F0.wireOp",EDGE,"E8.3"),sQuery(id+"F0.wireOp",EDGE,"E8.4"),sQuery(id+"F0.wireOp",EDGE,"E8.5"),sQuery(id+"F0.wireOp",EDGE,"E9"),sQuery(id+"F0.wireOp",EDGE,"E11"),sQuery(id+"F0.wireOp",EDGE,"E15.1.3"),sQuery(id+"F0.wireOp",EDGE,"E15.1.5"),sQuery(id+"F0.wireOp",EDGE,"E15.1.10"),sQuery(id+"F0.wireOp",EDGE,"E15.1.11"),sQuery(id+"F0.wireOp",EDGE,"E15.1.12"),subQ1,sQuery(id+"F0.wireOp",EDGE,"E15.1.17"),sQuery(id+"F0.wireOp",EDGE,"E15.1.19"),sQuery(id+"F0.wireOp",EDGE,"E15.1.24"),sQuery(id+"F0.wireOp",EDGE,"E15.1.25"),sQuery(id+"F0.wireOp",EDGE,"E15.1.29"),sQuery(id+"F0.wireOp",EDGE,"E15.1.30"),sQuery(id+"F0.wireOp",EDGE,"E15.1.32"),subQ0,sQuery(id+"F0.wireOp",EDGE,"E15.2.3"),sQuery(id+"F0.wireOp",EDGE,"E15.2.5"),sQuery(id+"F0.wireOp",EDGE,"E15.2.10"),sQuery(id+"F0.wireOp",EDGE,"E15.2.11"),sQuery(id+"F0.wireOp",EDGE,"E15.2.12"),sQuery(id+"F0.wireOp",EDGE,"E15.2.16"),sQuery(id+"F0.wireOp",EDGE,"E15.2.17"),sQuery(id+"F0.wireOp",EDGE,"E15.2.19"),sQuery(id+"F0.wireOp",EDGE,"E15.2.24"),sQuery(id+"F0.wireOp",EDGE,"E15.2.25"),sQuery(id+"F0.wireOp",EDGE,"E15.2.29"),sQuery(id+"F0.wireOp",EDGE,"E15.2.30"),sQuery(id+"F0.wireOp",EDGE,"E15.2.32"),sQuery(id+"F0.wireOp",EDGE,"E0")])],"isStart":false})],"blendedInto":[makeQuery(id+"F2.opExtrude","CAP_FACE",FACE,{"disambiguationData":[OSD([sQuery(id+"F0.wireOp",EDGE,"E2.0"),sQuery(id+"F0.wireOp",EDGE,"E2.1"),sQuery(id+"F0.wireOp",EDGE,"E2.2"),sQuery(id+"F0.wireOp",EDGE,"E2.3"),sQuery(id+"F0.wireOp",EDGE,"E2.4"),sQuery(id+"F0.wireOp",EDGE,"E2.5"),sQuery(id+"F0.wireOp",EDGE,"E8.1"),sQuery(id+"F0.wireOp",EDGE,"E8.2"),sQuery(id+"F0.wireOp",EDGE,"E8.3"),sQuery(id+"F0.wireOp",EDGE,"E8.4"),sQuery(id+"F0.wireOp",EDGE,"E8.5"),sQuery(id+"F0.wireOp",EDGE,"E9"),sQuery(id+"F0.wireOp",EDGE,"E11"),sQuery(id+"F0.wireOp",EDGE,"E15.1.3"),sQuery(id+"F0.wireOp",EDGE,"E15.1.5"),sQuery(id+"F0.wireOp",EDGE,"E15.1.10"),sQuery(id+"F0.wireOp",EDGE,"E15.1.11"),sQuery(id+"F0.wireOp",EDGE,"E15.1.12"),subQ1,sQuery(id+"F0.wireOp",EDGE,"E15.1.17"),sQuery(id+"F0.wireOp",EDGE,"E15.1.19"),sQuery(id+"F0.wireOp",EDGE,"E15.1.24"),sQuery(id+"F0.wireOp",EDGE,"E15.1.25"),sQuery(id+"F0.wireOp",EDGE,"E15.1.29"),sQuery(id+"F0.wireOp",EDGE,"E15.1.30"),sQuery(id+"F0.wireOp",EDGE,"E15.1.32"),subQ0,sQuery(id+"F0.wireOp",EDGE,"E15.2.3"),sQuery(id+"F0.wireOp",EDGE,"E15.2.5"),sQuery(id+"F0.wireOp",EDGE,"E15.2.10"),sQuery(id+"F0.wireOp",EDGE,"E15.2.11"),sQuery(id+"F0.wireOp",EDGE,"E15.2.12"),sQuery(id+"F0.wireOp",EDGE,"E15.2.16"),sQuery(id+"F0.wireOp",EDGE,"E15.2.17"),sQuery(id+"F0.wireOp",EDGE,"E15.2.19"),sQuery(id+"F0.wireOp",EDGE,"E15.2.24"),sQuery(id+"F0.wireOp",EDGE,"E15.2.25"),sQuery(id+"F0.wireOp",EDGE,"E15.2.29"),sQuery(id+"F0.wireOp",EDGE,"E15.2.30"),sQuery(id+"F0.wireOp",EDGE,"E15.2.32"),sQuery(id+"F0.wireOp",EDGE,"E0")])],"isStart":false})]});}
            var Q13;
            Q13=makeQuery(id+"F2.opExtrude","CAP_EDGE",EDGE,{"disambiguationData":[OSD([sQuery(id+"F0.wireOp",EDGE,"E15.1.17")])],"isStart":false});
            var Q14;
            Q14=makeQuery(id+"F2.opExtrude","CAP_EDGE",EDGE,{"disambiguationData":[OSD([sQuery(id+"F0.wireOp",EDGE,"E15.1.5")])],"isStart":false});
            var Q15;
            Q15=makeQuery(id+"F2.opExtrude","CAP_EDGE",EDGE,{"disambiguationData":[OSD([sQuery(id+"F0.wireOp",EDGE,"E15.1.19")])],"isStart":false});
            var Q16;
            Q16=makeQuery(id+"F2.opExtrude","CAP_EDGE",EDGE,{"disambiguationData":[OSD([sQuery(id+"F0.wireOp",EDGE,"E15.1.11")])],"isStart":false});
            var Q17;
            {var subQ0=sQuery(id+"F0.wireOp",EDGE,"E14");var subQ1=sQuery(id+"F0.wireOp",EDGE,"E15.1.16");Q17=makeQuery(id+"F3.opFillet","BLEND_EDGE",EDGE,{"blendedFrom":[makeQuery(id+"F2.opExtrude","SWEPT_EDGE",EDGE,{"disambiguationData":[OSD([subQ1,subQ0])]}),makeQuery(id+"F2.opExtrude","CAP_FACE",FACE,{"disambiguationData":[OSD([sQuery(id+"F0.wireOp",EDGE,"E2.0"),sQuery(id+"F0.wireOp",EDGE,"E2.1"),sQuery(id+"F0.wireOp",EDGE,"E2.2"),sQuery(id+"F0.wireOp",EDGE,"E2.3"),sQuery(id+"F0.wireOp",EDGE,"E2.4"),sQuery(id+"F0.wireOp",EDGE,"E2.5"),sQuery(id+"F0.wireOp",EDGE,"E8.1"),sQuery(id+"F0.wireOp",EDGE,"E8.2"),sQuery(id+"F0.wireOp",EDGE,"E8.3"),sQuery(id+"F0.wireOp",EDGE,"E8.4"),sQuery(id+"F0.wireOp",EDGE,"E8.5"),sQuery(id+"F0.wireOp",EDGE,"E9"),sQuery(id+"F0.wireOp",EDGE,"E11"),sQuery(id+"F0.wireOp",EDGE,"E15.1.3"),sQuery(id+"F0.wireOp",EDGE,"E15.1.5"),sQuery(id+"F0.wireOp",EDGE,"E15.1.10"),sQuery(id+"F0.wireOp",EDGE,"E15.1.11"),sQuery(id+"F0.wireOp",EDGE,"E15.1.12"),subQ1,sQuery(id+"F0.wireOp",EDGE,"E15.1.17"),sQuery(id+"F0.wireOp",EDGE,"E15.1.19"),sQuery(id+"F0.wireOp",EDGE,"E15.1.24"),sQuery(id+"F0.wireOp",EDGE,"E15.1.25"),sQuery(id+"F0.wireOp",EDGE,"E15.1.29"),sQuery(id+"F0.wireOp",EDGE,"E15.1.30"),sQuery(id+"F0.wireOp",EDGE,"E15.1.32"),subQ0,sQuery(id+"F0.wireOp",EDGE,"E15.2.3"),sQuery(id+"F0.wireOp",EDGE,"E15.2.5"),sQuery(id+"F0.wireOp",EDGE,"E15.2.10"),sQuery(id+"F0.wireOp",EDGE,"E15.2.11"),sQuery(id+"F0.wireOp",EDGE,"E15.2.12"),sQuery(id+"F0.wireOp",EDGE,"E15.2.16"),sQuery(id+"F0.wireOp",EDGE,"E15.2.17"),sQuery(id+"F0.wireOp",EDGE,"E15.2.19"),sQuery(id+"F0.wireOp",EDGE,"E15.2.24"),sQuery(id+"F0.wireOp",EDGE,"E15.2.25"),sQuery(id+"F0.wireOp",EDGE,"E15.2.29"),sQuery(id+"F0.wireOp",EDGE,"E15.2.30"),sQuery(id+"F0.wireOp",EDGE,"E15.2.32"),sQuery(id+"F0.wireOp",EDGE,"E0")])],"isStart":true})],"blendedInto":[makeQuery(id+"F2.opExtrude","CAP_FACE",FACE,{"disambiguationData":[OSD([sQuery(id+"F0.wireOp",EDGE,"E2.0"),sQuery(id+"F0.wireOp",EDGE,"E2.1"),sQuery(id+"F0.wireOp",EDGE,"E2.2"),sQuery(id+"F0.wireOp",EDGE,"E2.3"),sQuery(id+"F0.wireOp",EDGE,"E2.4"),sQuery(id+"F0.wireOp",EDGE,"E2.5"),sQuery(id+"F0.wireOp",EDGE,"E8.1"),sQuery(id+"F0.wireOp",EDGE,"E8.2"),sQuery(id+"F0.wireOp",EDGE,"E8.3"),sQuery(id+"F0.wireOp",EDGE,"E8.4"),sQuery(id+"F0.wireOp",EDGE,"E8.5"),sQuery(id+"F0.wireOp",EDGE,"E9"),sQuery(id+"F0.wireOp",EDGE,"E11"),sQuery(id+"F0.wireOp",EDGE,"E15.1.3"),sQuery(id+"F0.wireOp",EDGE,"E15.1.5"),sQuery(id+"F0.wireOp",EDGE,"E15.1.10"),sQuery(id+"F0.wireOp",EDGE,"E15.1.11"),sQuery(id+"F0.wireOp",EDGE,"E15.1.12"),subQ1,sQuery(id+"F0.wireOp",EDGE,"E15.1.17"),sQuery(id+"F0.wireOp",EDGE,"E15.1.19"),sQuery(id+"F0.wireOp",EDGE,"E15.1.24"),sQuery(id+"F0.wireOp",EDGE,"E15.1.25"),sQuery(id+"F0.wireOp",EDGE,"E15.1.29"),sQuery(id+"F0.wireOp",EDGE,"E15.1.30"),sQuery(id+"F0.wireOp",EDGE,"E15.1.32"),subQ0,sQuery(id+"F0.wireOp",EDGE,"E15.2.3"),sQuery(id+"F0.wireOp",EDGE,"E15.2.5"),sQuery(id+"F0.wireOp",EDGE,"E15.2.10"),sQuery(id+"F0.wireOp",EDGE,"E15.2.11"),sQuery(id+"F0.wireOp",EDGE,"E15.2.12"),sQuery(id+"F0.wireOp",EDGE,"E15.2.16"),sQuery(id+"F0.wireOp",EDGE,"E15.2.17"),sQuery(id+"F0.wireOp",EDGE,"E15.2.19"),sQuery(id+"F0.wireOp",EDGE,"E15.2.24"),sQuery(id+"F0.wireOp",EDGE,"E15.2.25"),sQuery(id+"F0.wireOp",EDGE,"E15.2.29"),sQuery(id+"F0.wireOp",EDGE,"E15.2.30"),sQuery(id+"F0.wireOp",EDGE,"E15.2.32"),sQuery(id+"F0.wireOp",EDGE,"E0")])],"isStart":true})]});}
            var Q18;
            Q18=makeQuery(id+"F2.opExtrude","CAP_EDGE",EDGE,{"disambiguationData":[OSD([sQuery(id+"F0.wireOp",EDGE,"E11")])],"isStart":true});
            var Q19;
            {var subQ0=sQuery(id+"F0.wireOp",EDGE,"E14");Q19=makeQuery(id+"F2.opExtrude","CAP_EDGE",EDGE,{"disambiguationData":[OSD([subQ0]),TDD([makeQuery(id+"F0.imprint","IMPRINT",EDGE,{"disambiguationData":[TD([[makeQuery(id+"F0.imprint","INTERSECT",VERTEX,{"derivedFrom":[sQuery(id+"F0.wireOp",EDGE,"E9"),subQ0]}),1.0]])],"derivedFrom":subQ0})])],"isStart":true});}
            var Q20;
            Q20=makeQuery(id+"F2.opExtrude","CAP_EDGE",EDGE,{"disambiguationData":[OSD([sQuery(id+"F0.wireOp",EDGE,"E15.1.5")])],"isStart":true});
            var Q21;
            Q21=makeQuery(id+"F2.opExtrude","CAP_EDGE",EDGE,{"disambiguationData":[OSD([sQuery(id+"F0.wireOp",EDGE,"E15.1.12")])],"isStart":true});
            var Q22;
            Q22=makeQuery(id+"F2.opExtrude","CAP_EDGE",EDGE,{"disambiguationData":[OSD([sQuery(id+"F0.wireOp",EDGE,"E15.1.17")])],"isStart":true});
            var Q23;
            Q23=makeQuery(id+"F2.opExtrude","CAP_EDGE",EDGE,{"disambiguationData":[OSD([sQuery(id+"F0.wireOp",EDGE,"E15.1.11")])],"isStart":true});
            var Q24;
            Q24=makeQuery(id+"F2.opExtrude","CAP_EDGE",EDGE,{"disambiguationData":[OSD([sQuery(id+"F0.wireOp",EDGE,"E15.1.19")])],"isStart":true});
            var Q25;
            Q25=makeQuery(id+"F2.opExtrude","CAP_EDGE",EDGE,{"disambiguationData":[OSD([sQuery(id+"F0.wireOp",EDGE,"E15.2.19")])],"isStart":true});
            var Q26;
            Q26=makeQuery(id+"F2.opExtrude","CAP_EDGE",EDGE,{"disambiguationData":[OSD([sQuery(id+"F0.wireOp",EDGE,"E15.2.11")])],"isStart":true});
            var Q27;
            Q27=makeQuery(id+"F2.opExtrude","CAP_EDGE",EDGE,{"disambiguationData":[OSD([sQuery(id+"F0.wireOp",EDGE,"E15.2.5")])],"isStart":true});
            var Q28;
            Q28=makeQuery(id+"F2.opExtrude","CAP_EDGE",EDGE,{"disambiguationData":[OSD([sQuery(id+"F0.wireOp",EDGE,"E15.2.12")])],"isStart":true});
            var Q29;
            Q29=makeQuery(id+"F2.opExtrude","CAP_EDGE",EDGE,{"disambiguationData":[OSD([sQuery(id+"F0.wireOp",EDGE,"E15.2.17")])],"isStart":true});
            var Q30;
            Q30=makeQuery(id+"F2.opExtrude","CAP_EDGE",EDGE,{"disambiguationData":[OSD([sQuery(id+"F0.wireOp",EDGE,"E8.1")])],"isStart":true});
            var Q31;
            Q31=makeQuery(id+"F2.opExtrude","CAP_EDGE",EDGE,{"disambiguationData":[OSD([sQuery(id+"F0.wireOp",EDGE,"E8.2")])],"isStart":true});
            var Q32;
            Q32=makeQuery(id+"F2.opExtrude","CAP_EDGE",EDGE,{"disambiguationData":[OSD([sQuery(id+"F0.wireOp",EDGE,"E8.3")])],"isStart":true});
            var Q33;
            Q33=makeQuery(id+"F2.opExtrude","CAP_EDGE",EDGE,{"disambiguationData":[OSD([sQuery(id+"F0.wireOp",EDGE,"E8.4")])],"isStart":true});
            var Q34;
            Q34=makeQuery(id+"F2.opExtrude","CAP_EDGE",EDGE,{"disambiguationData":[OSD([sQuery(id+"F0.wireOp",EDGE,"E8.5")])],"isStart":true});
            fillet(context, id + "F4", {"entities" : qUnion([Q0, Q1, Q2, Q3, Q4, Q5, Q6, Q7, Q8, Q9, Q10, Q11, Q12, Q13, Q14, Q15, Q16, Q17, Q18, Q19, Q20, Q21, Q22, Q23, Q24, Q25, Q26, Q27, Q28, Q29, Q30, Q31, Q32, Q33, Q34]), "radius" : 1 * mm, "tangentPropagation" : true, "allowEdgeOverflow" : false});
        }
        {
            var Q0;
            Q0 = qSketchRegion(id + "F1", true);
            extrude(context, id + "F5", {"entities" : qUnion([Q0]), "depth" : 7 * mm, "offsetDistance" : 25 * mm});
        }
        {
            var Q0;
            Q0=makeQuery(id+"F5.opExtrude","SWEPT_EDGE",EDGE,{"disambiguationData":[OSD([sQuery(id+"F1.wireOp",EDGE,"E30.1.8"),sQuery(id+"F1.wireOp",EDGE,"E30.2.21")])]});
            var Q1;
            Q1=makeQuery(id+"F5.opExtrude","SWEPT_EDGE",EDGE,{"disambiguationData":[OSD([sQuery(id+"F1.wireOp",EDGE,"E30.1.15"),sQuery(id+"F1.wireOp",EDGE,"E30.2.21")])]});
            var Q2;
            Q2=makeQuery(id+"F5.opExtrude","SWEPT_EDGE",EDGE,{"disambiguationData":[OSD([sQuery(id+"F1.wireOp",EDGE,"E27"),sQuery(id+"F1.wireOp",EDGE,"E30.2.6")])]});
            var Q3;
            Q3=makeQuery(id+"F5.opExtrude","SWEPT_EDGE",EDGE,{"disambiguationData":[OSD([sQuery(id+"F1.wireOp",EDGE,"E25"),sQuery(id+"F1.wireOp",EDGE,"E30.2.6")])]});
            var Q4;
            Q4=makeQuery(id+"F5.opExtrude","SWEPT_EDGE",EDGE,{"disambiguationData":[OSD([sQuery(id+"F1.wireOp",EDGE,"E30.2.3"),sQuery(id+"F1.wireOp",EDGE,"E30.2.15")])]});
            var Q5;
            Q5=makeQuery(id+"F5.opExtrude","SWEPT_EDGE",EDGE,{"disambiguationData":[OSD([sQuery(id+"F1.wireOp",EDGE,"E30.2.3"),sQuery(id+"F1.wireOp",EDGE,"E30.2.8")])]});
            fillet(context, id + "F6", {"entities" : qUnion([Q0, Q1, Q2, Q3, Q4, Q5]), "radius" : 3 * mm, "tangentPropagation" : true, "allowEdgeOverflow" : false});
        }
        {
            var Q0;
            Q0=makeQuery(id+"F5.opExtrude","SWEPT_EDGE",EDGE,{"disambiguationData":[OSD([sQuery(id+"F1.wireOp",EDGE,"E30.2.29"),sQuery(id+"F1.wireOp",EDGE,"E30.2.31")])]});
            var Q1;
            Q1=makeQuery(id+"F5.opExtrude","SWEPT_EDGE",EDGE,{"disambiguationData":[OSD([sQuery(id+"F1.wireOp",EDGE,"E30.2.17"),sQuery(id+"F1.wireOp",EDGE,"E30.2.29")])]});
            var Q2;
            Q2=makeQuery(id+"F5.opExtrude","SWEPT_EDGE",EDGE,{"disambiguationData":[OSD([sQuery(id+"F1.wireOp",EDGE,"E30.2.28"),sQuery(id+"F1.wireOp",EDGE,"E30.2.31")])]});
            var Q3;
            Q3=makeQuery(id+"F5.opExtrude","SWEPT_EDGE",EDGE,{"disambiguationData":[OSD([sQuery(id+"F1.wireOp",EDGE,"E30.2.10"),sQuery(id+"F1.wireOp",EDGE,"E30.2.28")])]});
            var Q4;
            Q4=makeQuery(id+"F5.opExtrude","SWEPT_EDGE",EDGE,{"disambiguationData":[OSD([sQuery(id+"F1.wireOp",EDGE,"E30.1.28"),sQuery(id+"F1.wireOp",EDGE,"E30.1.31")])]});
            var Q5;
            Q5=makeQuery(id+"F5.opExtrude","SWEPT_EDGE",EDGE,{"disambiguationData":[OSD([sQuery(id+"F1.wireOp",EDGE,"E30.1.29"),sQuery(id+"F1.wireOp",EDGE,"E30.1.31")])]});
            var Q6;
            Q6=makeQuery(id+"F5.opExtrude","SWEPT_EDGE",EDGE,{"disambiguationData":[OSD([sQuery(id+"F1.wireOp",EDGE,"E30.1.17"),sQuery(id+"F1.wireOp",EDGE,"E30.1.29")])]});
            var Q7;
            Q7=makeQuery(id+"F5.opExtrude","SWEPT_EDGE",EDGE,{"disambiguationData":[OSD([sQuery(id+"F1.wireOp",EDGE,"E24.1"),sQuery(id+"F1.wireOp",EDGE,"E24.2")])]});
            var Q8;
            Q8=makeQuery(id+"F5.opExtrude","SWEPT_EDGE",EDGE,{"disambiguationData":[OSD([sQuery(id+"F1.wireOp",EDGE,"E24.2"),sQuery(id+"F1.wireOp",EDGE,"E24.3")])]});
            var Q9;
            Q9=makeQuery(id+"F5.opExtrude","SWEPT_EDGE",EDGE,{"disambiguationData":[OSD([sQuery(id+"F1.wireOp",EDGE,"E24.3"),sQuery(id+"F1.wireOp",EDGE,"E24.4")])]});
            var Q10;
            Q10=makeQuery(id+"F5.opExtrude","SWEPT_EDGE",EDGE,{"disambiguationData":[OSD([sQuery(id+"F1.wireOp",EDGE,"E24.4"),sQuery(id+"F1.wireOp",EDGE,"E24.5")])]});
            var Q11;
            Q11=makeQuery(id+"F5.opExtrude","SWEPT_EDGE",EDGE,{"disambiguationData":[OSD([sQuery(id+"F1.wireOp",EDGE,"E30.1.10"),sQuery(id+"F1.wireOp",EDGE,"E30.1.28")])]});
            fillet(context, id + "F7", {"entities" : qUnion([Q0, Q1, Q2, Q3, Q4, Q5, Q6, Q7, Q8, Q9, Q10, Q11]), "radius" : 2 * mm, "tangentPropagation" : true, "allowEdgeOverflow" : false});
        }
    });
